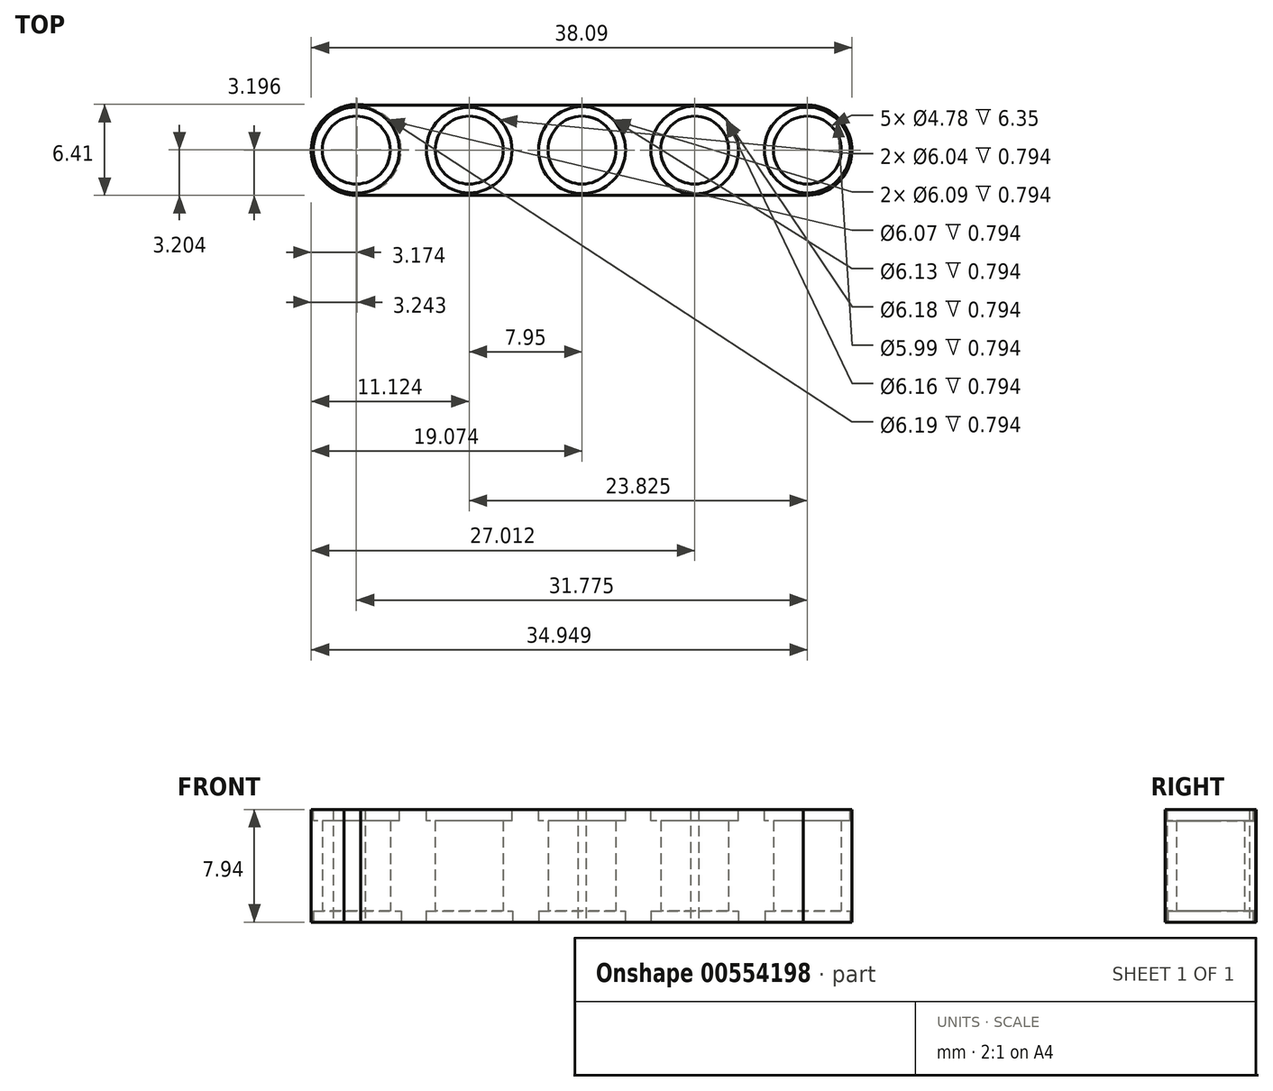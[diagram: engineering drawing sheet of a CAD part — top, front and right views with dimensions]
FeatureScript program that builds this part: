
annotation { "Feature Type Name" : "Feature", "Feature Type Description" : "" }
export const myFeature = defineFeature(function(context is Context, id is Id, definition is map)
    precondition{}
    {
        {
            var Q0;
            Q0=qCreatedBy(makeId("Top.planeOp"),FACE);
            var sketch = newSketch(context, id + "F0", { "sketchPlane" : qUnion([Q0])});
            skArc(sketch, "E0", {"start": v(-3.42, 0) * mm, "mid": v(0, 3.2) * mm, "end": v(-3.46, 6.35) * mm});
            skArc(sketch, "E1", {"start": v(-34.29, 6.35) * mm, "mid": v(-38.05, 3.35) * mm, "end": v(-34.6, 0) * mm});
            skLineSegment(sketch, "E2", {"start": v(-34.29, 6.35) * mm, "end": v(-3.46, 6.35) * mm});
            skLineSegment(sketch, "E3", {"start": v(-34.6, 0) * mm, "end": v(-3.42, 0) * mm});
            skCircle(sketch, "E4", {"center": v(-19.02, 3.19) * mm, "radius": 3.18 * mm});
            skCircle(sketch, "E5", {"center": v(-19.02, 3.19) * mm, "radius": 2.4 * mm});
            skCircle(sketch, "E6.1.0.0", {"center": v(-11.08, 3.19) * mm, "radius": 3.18 * mm});
            skCircle(sketch, "E6.1.0.1", {"center": v(-11.08, 3.19) * mm, "radius": 2.4 * mm});
            skCircle(sketch, "E6.2.0.0", {"center": v(-3.14, 3.19) * mm, "radius": 3.18 * mm});
            skCircle(sketch, "E6.2.0.1", {"center": v(-3.14, 3.19) * mm, "radius": 2.4 * mm});
            skLineSegment(sketch, "E6.direction1", {"start": v(-19.02, 3.19) * mm, "end": v(-11.08, 3.19) * mm, "construction": true});
            skCircle(sketch, "E7.1.0.0", {"center": v(-26.97, 3.19) * mm, "radius": 3.18 * mm});
            skCircle(sketch, "E7.1.0.1", {"center": v(-26.97, 3.19) * mm, "radius": 2.4 * mm});
            skCircle(sketch, "E7.2.0.0", {"center": v(-34.92, 3.19) * mm, "radius": 3.18 * mm});
            skCircle(sketch, "E7.2.0.1", {"center": v(-34.92, 3.19) * mm, "radius": 2.4 * mm});
            skLineSegment(sketch, "E7.direction1", {"start": v(-19.02, 3.19) * mm, "end": v(-26.97, 3.19) * mm, "construction": true});
            skSolve(sketch);
        }
        {
            var Q0;
            {var subQ0=sQuery(id+"F0.wireOp",EDGE,"E6.2.0.0");var subQ1=sQuery(id+"F0.wireOp",EDGE,"E0");var subQ2=makeQuery(id+"F0.imprint","INTERSECT",VERTEX,{"disambiguationData":[OD(0.0)],"derivedFrom":[subQ1,subQ0]});Q0=makeQuery(id+"F0.imprint","IMPRINT",FACE,{"disambiguationData":[TD([[makeQuery(id+"F0.imprint","IMPRINT",EDGE,{"disambiguationData":[TD([[subQ2,-1.0]])],"derivedFrom":subQ1}),-1.0]])]});}
            var Q1;
            {var subQ0=sQuery(id+"F0.wireOp",EDGE,"E7.2.0.0");var subQ1=sQuery(id+"F0.wireOp",EDGE,"E1");var subQ2=makeQuery(id+"F0.imprint","INTERSECT",VERTEX,{"disambiguationData":[OD(0.0)],"derivedFrom":[subQ1,subQ0]});Q1=makeQuery(id+"F0.imprint","IMPRINT",FACE,{"disambiguationData":[TD([[makeQuery(id+"F0.imprint","IMPRINT",EDGE,{"disambiguationData":[TD([[subQ2,-1.0]])],"derivedFrom":subQ1}),-1.0]])]});}
            var Q2;
            {var subQ0=sQuery(id+"F0.wireOp",EDGE,"E7.1.0.0");var subQ1=sQuery(id+"F0.wireOp",EDGE,"E2");var subQ2=makeQuery(id+"F0.imprint","INTERSECT",VERTEX,{"disambiguationData":[OD(0.0)],"derivedFrom":[subQ1,subQ0]});Q2=makeQuery(id+"F0.imprint","IMPRINT",FACE,{"disambiguationData":[TD([[makeQuery(id+"F0.imprint","IMPRINT",EDGE,{"disambiguationData":[TD([[subQ2,-1.0]])],"derivedFrom":subQ1}),1.0]])]});}
            var Q3;
            {var subQ0=sQuery(id+"F0.wireOp",EDGE,"E4");var subQ1=sQuery(id+"F0.wireOp",EDGE,"E2");var subQ2=makeQuery(id+"F0.imprint","INTERSECT",VERTEX,{"disambiguationData":[OD(0.0)],"derivedFrom":[subQ1,subQ0]});Q3=makeQuery(id+"F0.imprint","IMPRINT",FACE,{"disambiguationData":[TD([[makeQuery(id+"F0.imprint","IMPRINT",EDGE,{"disambiguationData":[TD([[subQ2,-1.0]])],"derivedFrom":subQ1}),1.0]])]});}
            var Q4;
            {var subQ0=sQuery(id+"F0.wireOp",EDGE,"E6.1.0.0");var subQ1=sQuery(id+"F0.wireOp",EDGE,"E2");var subQ2=makeQuery(id+"F0.imprint","INTERSECT",VERTEX,{"disambiguationData":[OD(0.0)],"derivedFrom":[subQ1,subQ0]});Q4=makeQuery(id+"F0.imprint","IMPRINT",FACE,{"disambiguationData":[TD([[makeQuery(id+"F0.imprint","IMPRINT",EDGE,{"disambiguationData":[TD([[subQ2,-1.0]])],"derivedFrom":subQ1}),1.0]])]});}
            var Q5;
            {var subQ14=sQuery(id+"F0.wireOp",EDGE,"E3");Q5=makeQuery(id+"F0.imprint","IMPRINT",FACE,{"disambiguationData":[TD([[makeQuery(id+"F0.imprint","IMPRINT",EDGE,{"derivedFrom":subQ14}),1.0]])]});}
            var Q6;
            Q6=makeQuery(id+"F0.imprint","IMPRINT",FACE,{"disambiguationData":[TD([[makeQuery(id+"F0.imprint","IMPRINT",EDGE,{"derivedFrom":sQuery(id+"F0.wireOp",EDGE,"E7.2.0.1")}),-1.0]])]});
            var Q7;
            Q7=makeQuery(id+"F0.imprint","IMPRINT",FACE,{"disambiguationData":[TD([[makeQuery(id+"F0.imprint","IMPRINT",EDGE,{"derivedFrom":sQuery(id+"F0.wireOp",EDGE,"E7.1.0.1")}),-1.0]])]});
            var Q8;
            Q8=makeQuery(id+"F0.imprint","IMPRINT",FACE,{"disambiguationData":[TD([[makeQuery(id+"F0.imprint","IMPRINT",EDGE,{"derivedFrom":sQuery(id+"F0.wireOp",EDGE,"E5")}),-1.0]])]});
            var Q9;
            Q9=makeQuery(id+"F0.imprint","IMPRINT",FACE,{"disambiguationData":[TD([[makeQuery(id+"F0.imprint","IMPRINT",EDGE,{"derivedFrom":sQuery(id+"F0.wireOp",EDGE,"E6.1.0.1")}),-1.0]])]});
            var Q10;
            Q10=makeQuery(id+"F0.imprint","IMPRINT",FACE,{"disambiguationData":[TD([[makeQuery(id+"F0.imprint","IMPRINT",EDGE,{"derivedFrom":sQuery(id+"F0.wireOp",EDGE,"E6.2.0.1")}),-1.0]])]});
            extrude(context, id + "F1", {"entities" : qUnion([Q0, Q1, Q2, Q3, Q4, Q5, Q6, Q7, Q8, Q9, Q10]), "depth" : 7.94 * mm, "offsetDistance" : 25.4 * mm});
        }
        {
            var Q0;
            Q0=makeQuery(id+"F1.opExtrude","CAP_FACE",FACE,{"disambiguationData":[OSD([sQuery(id+"F0.wireOp",EDGE,"E0"),sQuery(id+"F0.wireOp",EDGE,"E1"),sQuery(id+"F0.wireOp",EDGE,"E2"),sQuery(id+"F0.wireOp",EDGE,"E3"),sQuery(id+"F0.wireOp",EDGE,"E4"),sQuery(id+"F0.wireOp",EDGE,"E5"),sQuery(id+"F0.wireOp",EDGE,"E6.1.0.0"),sQuery(id+"F0.wireOp",EDGE,"E6.1.0.1"),sQuery(id+"F0.wireOp",EDGE,"E6.2.0.0"),sQuery(id+"F0.wireOp",EDGE,"E6.2.0.1"),sQuery(id+"F0.wireOp",EDGE,"E7.1.0.0"),sQuery(id+"F0.wireOp",EDGE,"E7.1.0.1"),sQuery(id+"F0.wireOp",EDGE,"E7.2.0.0"),sQuery(id+"F0.wireOp",EDGE,"E7.2.0.1")])],"isStart":false});
            var sketch = newSketch(context, id + "F2", { "sketchPlane" : qUnion([Q0])});
            skCircle(sketch, "E8", {"center": v(-34.92, 3.19) * mm, "radius": 3.04 * mm});
            skCircle(sketch, "E9", {"center": v(-26.97, 3.19) * mm, "radius": 3.02 * mm});
            skCircle(sketch, "E10", {"center": v(-19.02, 3.19) * mm, "radius": 3.06 * mm});
            skCircle(sketch, "E11", {"center": v(-11.08, 3.19) * mm, "radius": 3.1 * mm});
            skCircle(sketch, "E12", {"center": v(-3.14, 3.19) * mm, "radius": 3.02 * mm});
            skSolve(sketch);
        }
        {
            var Q0;
            Q0=makeQuery(id+"F2.imprint","IMPRINT",FACE,{"disambiguationData":[TD([[makeQuery(id+"F2.imprint","IMPRINT",EDGE,{"derivedFrom":sQuery(id+"F2.wireOp",EDGE,"E12")}),1.0]])]});
            var Q1;
            Q1=makeQuery(id+"F2.imprint","IMPRINT",FACE,{"disambiguationData":[TD([[makeQuery(id+"F2.imprint","IMPRINT",EDGE,{"derivedFrom":sQuery(id+"F2.wireOp",EDGE,"E11")}),1.0]])]});
            var Q2;
            Q2=makeQuery(id+"F2.imprint","IMPRINT",FACE,{"disambiguationData":[TD([[makeQuery(id+"F2.imprint","IMPRINT",EDGE,{"derivedFrom":sQuery(id+"F2.wireOp",EDGE,"E10")}),1.0]])]});
            var Q3;
            Q3=makeQuery(id+"F2.imprint","IMPRINT",FACE,{"disambiguationData":[TD([[makeQuery(id+"F2.imprint","IMPRINT",EDGE,{"derivedFrom":sQuery(id+"F2.wireOp",EDGE,"E9")}),1.0]])]});
            var Q4;
            Q4=makeQuery(id+"F2.imprint","IMPRINT",FACE,{"disambiguationData":[TD([[makeQuery(id+"F2.imprint","IMPRINT",EDGE,{"derivedFrom":sQuery(id+"F2.wireOp",EDGE,"E8")}),1.0]])]});
            extrude(context, id + "F3", {"entities" : qUnion([Q0, Q1, Q2, Q3, Q4]), "operationType" : NewBodyOperationType.REMOVE, "oppositeDirection" : true, "depth" : 0.8 * mm, "offsetDistance" : 25.4 * mm});
        }
        {
            var Q0;
            Q0=makeQuery(id+"F1.opExtrude","CAP_FACE",FACE,{"disambiguationData":[OSD([sQuery(id+"F0.wireOp",EDGE,"E0"),sQuery(id+"F0.wireOp",EDGE,"E1"),sQuery(id+"F0.wireOp",EDGE,"E2"),sQuery(id+"F0.wireOp",EDGE,"E3"),sQuery(id+"F0.wireOp",EDGE,"E4"),sQuery(id+"F0.wireOp",EDGE,"E5"),sQuery(id+"F0.wireOp",EDGE,"E6.1.0.0"),sQuery(id+"F0.wireOp",EDGE,"E6.1.0.1"),sQuery(id+"F0.wireOp",EDGE,"E6.2.0.0"),sQuery(id+"F0.wireOp",EDGE,"E6.2.0.1"),sQuery(id+"F0.wireOp",EDGE,"E7.1.0.0"),sQuery(id+"F0.wireOp",EDGE,"E7.1.0.1"),sQuery(id+"F0.wireOp",EDGE,"E7.2.0.0"),sQuery(id+"F0.wireOp",EDGE,"E7.2.0.1")])],"isStart":true});
            var sketch = newSketch(context, id + "F4", { "sketchPlane" : qUnion([Q0])});
            skCircle(sketch, "E13", {"center": v(-34.85, -3.2) * mm, "radius": 3.1 * mm});
            skCircle(sketch, "E14", {"center": v(-3.14, -3.19) * mm, "radius": 3 * mm});
            skCircle(sketch, "E15", {"center": v(-26.97, -3.19) * mm, "radius": 3.04 * mm});
            skCircle(sketch, "E16", {"center": v(-19.02, -3.19) * mm, "radius": 3.04 * mm});
            skCircle(sketch, "E17", {"center": v(-11.08, -3.19) * mm, "radius": 3.08 * mm});
            skSolve(sketch);
        }
        {
            var Q0;
            Q0=makeQuery(id+"F4.imprint","IMPRINT",FACE,{"disambiguationData":[TD([[makeQuery(id+"F4.imprint","IMPRINT",EDGE,{"derivedFrom":sQuery(id+"F4.wireOp",EDGE,"E13")}),1.0]])]});
            var Q1;
            Q1=makeQuery(id+"F4.imprint","IMPRINT",FACE,{"disambiguationData":[TD([[makeQuery(id+"F4.imprint","IMPRINT",EDGE,{"derivedFrom":sQuery(id+"F4.wireOp",EDGE,"E15")}),1.0]])]});
            var Q2;
            Q2=makeQuery(id+"F4.imprint","IMPRINT",FACE,{"disambiguationData":[TD([[makeQuery(id+"F4.imprint","IMPRINT",EDGE,{"derivedFrom":sQuery(id+"F4.wireOp",EDGE,"E16")}),1.0]])]});
            var Q3;
            Q3=makeQuery(id+"F4.imprint","IMPRINT",FACE,{"disambiguationData":[TD([[makeQuery(id+"F4.imprint","IMPRINT",EDGE,{"derivedFrom":sQuery(id+"F4.wireOp",EDGE,"E17")}),1.0]])]});
            var Q4;
            Q4=makeQuery(id+"F4.imprint","IMPRINT",FACE,{"disambiguationData":[TD([[makeQuery(id+"F4.imprint","IMPRINT",EDGE,{"derivedFrom":sQuery(id+"F4.wireOp",EDGE,"E14")}),1.0]])]});
            extrude(context, id + "F5", {"entities" : qUnion([Q0, Q1, Q2, Q3, Q4]), "operationType" : NewBodyOperationType.REMOVE, "oppositeDirection" : true, "depth" : 0.8 * mm, "offsetDistance" : 25.4 * mm});
        }
    });
